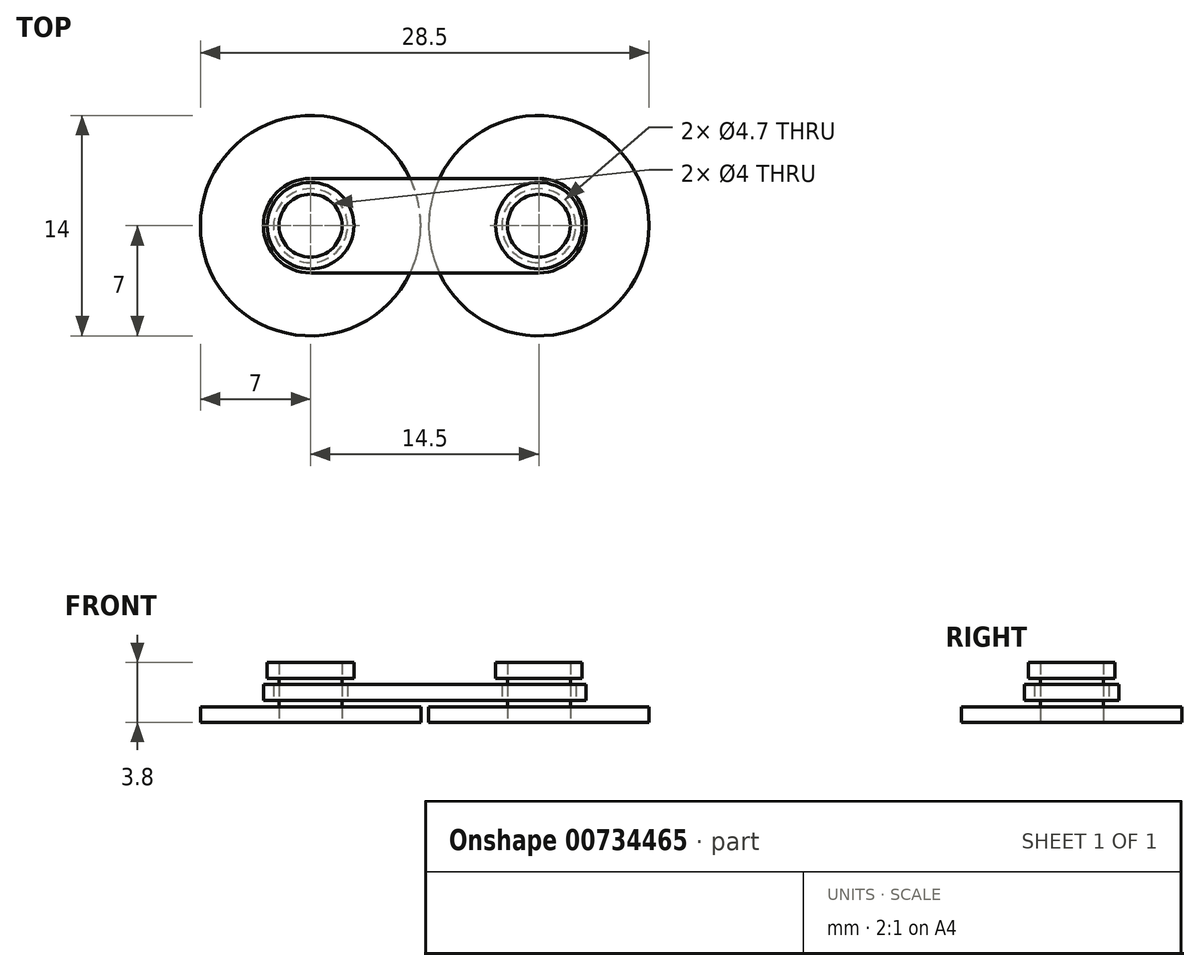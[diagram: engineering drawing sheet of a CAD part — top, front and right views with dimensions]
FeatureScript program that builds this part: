
annotation { "Feature Type Name" : "Feature", "Feature Type Description" : "" }
export const myFeature = defineFeature(function(context is Context, id is Id, definition is map)
    precondition{}
    {
        {
            var Q0;
            Q0=qCreatedBy(makeId("Top.planeOp"),FACE);
            var sketch = newSketch(context, id + "F0", { "sketchPlane" : qUnion([Q0])});
            skCircle(sketch, "E0", {"center": v(-7.25, 0) * mm, "radius": 7 * mm});
            skCircle(sketch, "E1", {"center": v(7.25, 0) * mm, "radius": 7 * mm});
            skCircle(sketch, "E2", {"center": v(-7.25, 0) * mm, "radius": 2 * mm});
            skCircle(sketch, "E3", {"center": v(7.25, 0) * mm, "radius": 2 * mm});
            skSolve(sketch);
        }
        {
            var Q0;
            Q0=makeQuery(id+"F0.imprint","IMPRINT",FACE,{"disambiguationData":[TD([[makeQuery(id+"F0.imprint","IMPRINT",EDGE,{"derivedFrom":sQuery(id+"F0.wireOp",EDGE,"E0")}),1.0]])]});
            var Q1;
            Q1=makeQuery(id+"F0.imprint","IMPRINT",FACE,{"disambiguationData":[TD([[makeQuery(id+"F0.imprint","IMPRINT",EDGE,{"derivedFrom":sQuery(id+"F0.wireOp",EDGE,"E1")}),1.0]])]});
            extrude(context, id + "F1", {"entities" : qUnion([Q0, Q1]), "depth" : 1 * mm, "offsetDistance" : 25 * mm});
        }
        {
            var Q0;
            Q0=makeQuery(id+"F0.imprint","IMPRINT",FACE,{"disambiguationData":[TD([[makeQuery(id+"F0.imprint","IMPRINT",EDGE,{"derivedFrom":sQuery(id+"F0.wireOp",EDGE,"E2")}),1.0]])]});
            var Q1;
            Q1=makeQuery(id+"F0.imprint","IMPRINT",FACE,{"disambiguationData":[TD([[makeQuery(id+"F0.imprint","IMPRINT",EDGE,{"derivedFrom":sQuery(id+"F0.wireOp",EDGE,"E3")}),1.0]])]});
            extrude(context, id + "F2", {"entities" : qUnion([Q0, Q1]), "depth" : 3.8 * mm, "offsetDistance" : 25 * mm});
        }
        {
            var Q0;
            Q0=qCreatedBy(makeId("Top.planeOp"),FACE);
            cPlane(context, id + "F3", {"entities" : qUnion([Q0]), "cplaneType" : CPlaneType.OFFSET, "offset" : 1.4 * mm, "width" : 150 * mm, "height" : 150 * mm});
        }
        {
            var Q0;
            Q0=qCreatedBy(id+"F3.planeOp",FACE);
            var sketch = newSketch(context, id + "F4", { "sketchPlane" : qUnion([Q0])});
            skCircle(sketch, "E4", {"center": v(-7.25, 0) * mm, "radius": 3 * mm});
            skCircle(sketch, "E5", {"center": v(7.25, 0) * mm, "radius": 3 * mm});
            skLineSegment(sketch, "E6", {"start": v(-7.25, -3) * mm, "end": v(7.25, -3) * mm});
            skLineSegment(sketch, "E7", {"start": v(-7.25, 3) * mm, "end": v(7.25, 3) * mm});
            skCircle(sketch, "E8", {"center": v(-7.25, 0) * mm, "radius": 2.35 * mm});
            skCircle(sketch, "E9", {"center": v(7.25, 0) * mm, "radius": 2.35 * mm});
            skSolve(sketch);
        }
        {
            var Q0;
            Q0 = qSketchRegion(id + "F4", true);
            extrude(context, id + "F5", {"entities" : qUnion([Q0]), "depth" : 1 * mm, "offsetDistance" : 25 * mm});
        }
        {
            var Q0;
            Q0=makeQuery(id+"F2.opExtrude","CAP_FACE",FACE,{"disambiguationData":[OSD([sQuery(id+"F0.wireOp",EDGE,"E2")])],"isStart":false});
            var sketch = newSketch(context, id + "F6", { "sketchPlane" : qUnion([Q0])});
            skCircle(sketch, "E10", {"center": v(-7.25, 0) * mm, "radius": 2.75 * mm});
            skCircle(sketch, "E11", {"center": v(7.25, 0) * mm, "radius": 2.75 * mm});
            skSolve(sketch);
        }
        {
            var Q0;
            Q0 = qSketchRegion(id + "F6", true);
            extrude(context, id + "F7", {"entities" : qUnion([Q0]), "oppositeDirection" : true, "depth" : 1 * mm, "offsetDistance" : 25 * mm});
        }
    });
